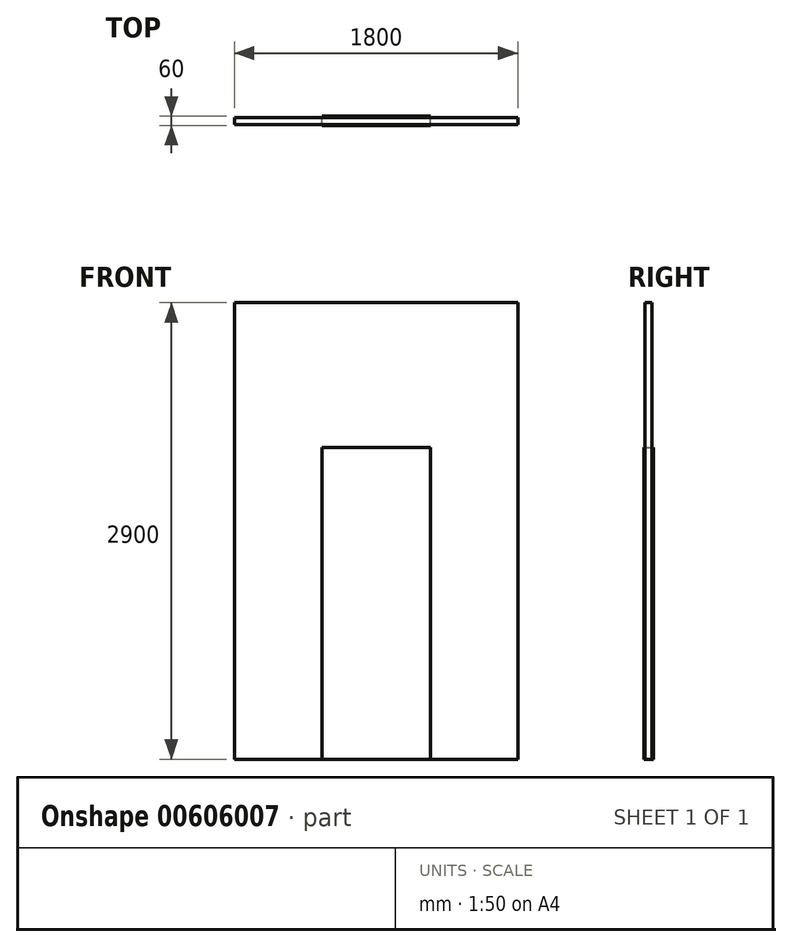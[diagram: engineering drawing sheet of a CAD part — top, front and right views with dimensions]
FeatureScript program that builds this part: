
annotation { "Feature Type Name" : "Feature", "Feature Type Description" : "" }
export const myFeature = defineFeature(function(context is Context, id is Id, definition is map)
    precondition{}
    {
        {
            var Q0;
            Q0=qCreatedBy(makeId("Top.planeOp"),FACE);
            var sketch = newSketch(context, id + "F0", { "sketchPlane" : qUnion([Q0])});
            skLineSegment(sketch, "E0.bottom", {"start": v(900, -22) * mm, "end": v(-900, -22) * mm});
            skLineSegment(sketch, "E0.top", {"start": v(900, 22) * mm, "end": v(-900, 22) * mm});
            skLineSegment(sketch, "E0.left", {"start": v(900, -22) * mm, "end": v(900, 22) * mm});
            skLineSegment(sketch, "E0.right", {"start": v(-900, -22) * mm, "end": v(-900, 22) * mm});
            skPoint(sketch, "E0.middle", {"position": v(0, 0) * mm});
            skLineSegment(sketch, "E1.bottom", {"start": v(345, -30) * mm, "end": v(-345, -30) * mm});
            skLineSegment(sketch, "E1.top", {"start": v(345, 30) * mm, "end": v(-345, 30) * mm});
            skLineSegment(sketch, "E1.left", {"start": v(345, -30) * mm, "end": v(345, 30) * mm});
            skLineSegment(sketch, "E1.right", {"start": v(-345, -30) * mm, "end": v(-345, 30) * mm});
            skSolve(sketch);
        }
        {
            var Q0;
            Q0=makeQuery(id+"F0.imprint","IMPRINT",FACE,{"disambiguationData":[TD([[makeQuery(id+"F0.imprint","IMPRINT",EDGE,{"derivedFrom":sQuery(id+"F0.wireOp",EDGE,"E0.bottom")}),-1.0]])]});
            extrude(context, id + "F1", {"entities" : qUnion([Q0]), "depth" : 2900 * mm, "offsetDistance" : 25 * mm});
        }
        {
            var Q0;
            {var subQ5=sQuery(id+"F0.wireOp",EDGE,"E1.top");Q0=makeQuery(id+"F0.imprint","IMPRINT",FACE,{"disambiguationData":[TD([[makeQuery(id+"F0.imprint","IMPRINT",EDGE,{"derivedFrom":subQ5}),1.0]])]});}
            var Q1;
            {var subQ0=sQuery(id+"F0.wireOp",EDGE,"E1.left");var subQ1=sQuery(id+"F0.wireOp",EDGE,"E0.bottom");var subQ2=makeQuery(id+"F0.imprint","INTERSECT",VERTEX,{"derivedFrom":[subQ1,subQ0]});Q1=makeQuery(id+"F0.imprint","IMPRINT",FACE,{"disambiguationData":[TD([[makeQuery(id+"F0.imprint","IMPRINT",EDGE,{"disambiguationData":[TD([[subQ2,-1.0]])],"derivedFrom":subQ1}),-1.0]])]});}
            var Q2;
            {var subQ5=sQuery(id+"F0.wireOp",EDGE,"E1.bottom");Q2=makeQuery(id+"F0.imprint","IMPRINT",FACE,{"disambiguationData":[TD([[makeQuery(id+"F0.imprint","IMPRINT",EDGE,{"derivedFrom":subQ5}),-1.0]])]});}
            extrude(context, id + "F2", {"entities" : qUnion([Q0, Q1, Q2]), "depth" : 1980 * mm, "offsetDistance" : 25 * mm});
        }
    });
